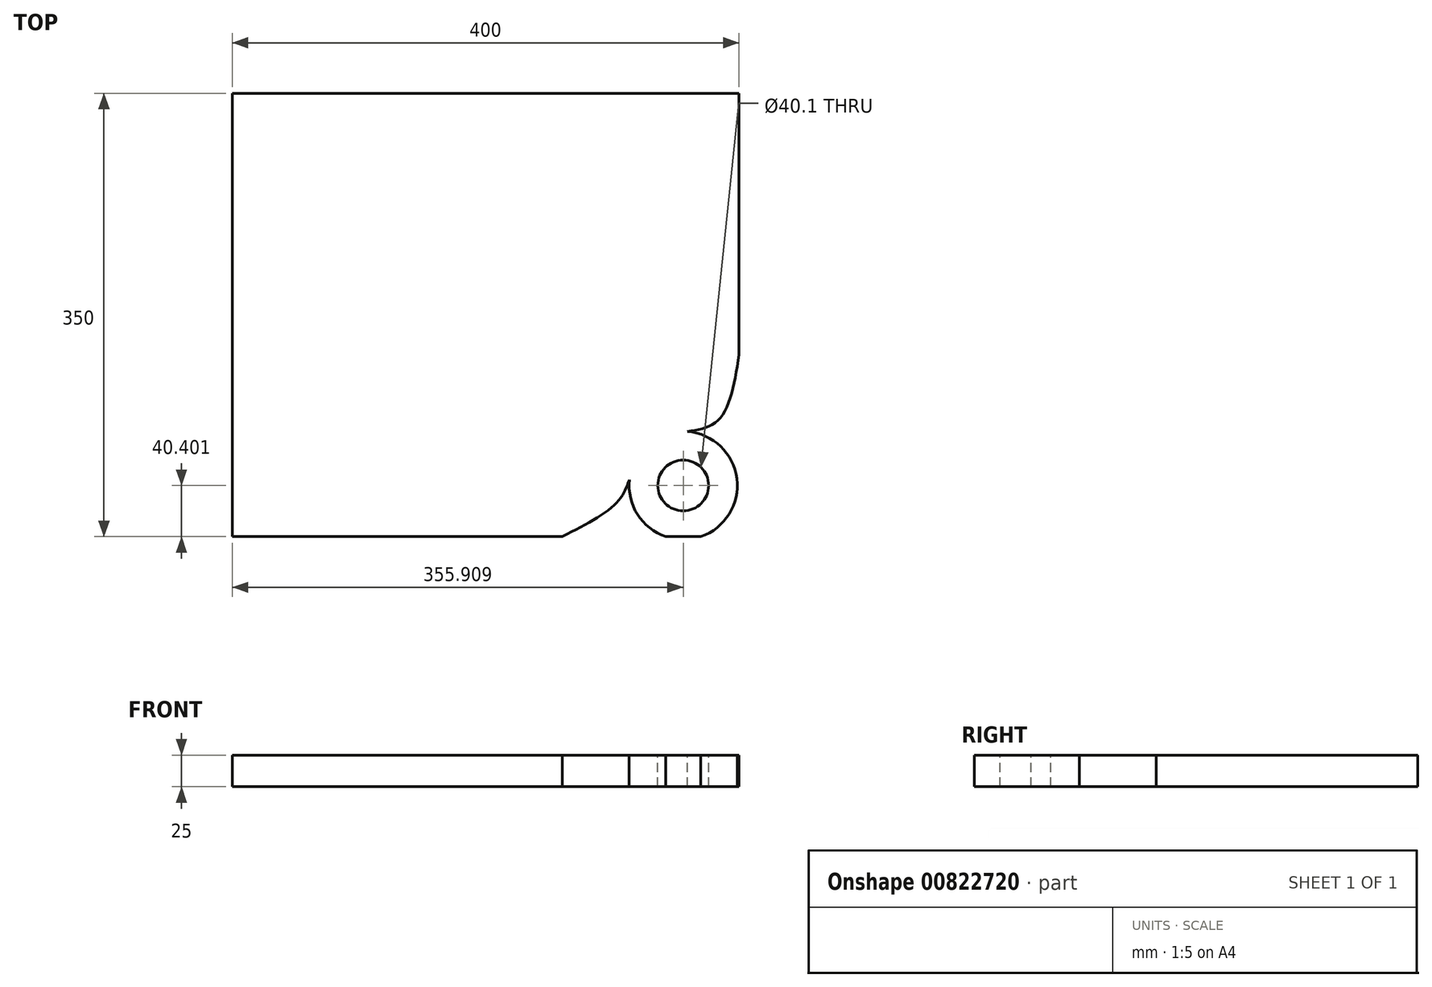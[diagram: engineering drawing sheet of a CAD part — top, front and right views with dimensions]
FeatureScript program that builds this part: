
annotation { "Feature Type Name" : "Feature", "Feature Type Description" : "" }
export const myFeature = defineFeature(function(context is Context, id is Id, definition is map)
    precondition{}
    {
        {
            var Q0;
            Q0=qCreatedBy(makeId("Top.planeOp"),FACE);
            var sketch = newSketch(context, id + "F0", { "sketchPlane" : qUnion([Q0])});
            skLineSegment(sketch, "E0.bottom", {"start": v(-344.67, 317.96) * mm, "end": v(55.33, 317.96) * mm});
            skLineSegment(sketch, "E0.top", {"start": v(-344.67, -32.04) * mm, "end": v(55.33, -32.04) * mm});
            skLineSegment(sketch, "E0.left", {"start": v(-344.67, 317.96) * mm, "end": v(-344.67, -32.04) * mm});
            skLineSegment(sketch, "E0.right", {"start": v(55.33, 317.96) * mm, "end": v(55.33, -32.04) * mm});
            skSolve(sketch);
        }
        {
            var Q0;
            Q0 = qSketchRegion(id + "F0", true);
            extrude(context, id + "F1", {"entities" : qUnion([Q0]), "depth" : 25 * mm, "offsetDistance" : 25 * mm});
        }
        {
            var Q0;
            Q0=makeQuery(id+"F1.opExtrude","CAP_FACE",FACE,{"disambiguationData":[OSD([sQuery(id+"F0.wireOp",EDGE,"E0.bottom"),sQuery(id+"F0.wireOp",EDGE,"E0.top"),sQuery(id+"F0.wireOp",EDGE,"E0.left"),sQuery(id+"F0.wireOp",EDGE,"E0.right")])],"isStart":false});
            var sketch = newSketch(context, id + "F2", { "sketchPlane" : qUnion([Q0])});
            skCircle(sketch, "E1", {"center": v(11.24, 8.36) * mm, "radius": 42.72 * mm});
            skFitSpline(sketch, "E2", {"points": [v(14.67, 50.94) * mm, v(39.8, 60.95) * mm, v(55.33, 111.58) * mm], "startDerivative": vector(67.32, 10.88) * mm, "endDerivative": vector(16.8, 105.15) * mm});
            skFitSpline(sketch, "E3", {"points": [v(-31.24, 12.86) * mm, v(-41.35, -5.27) * mm, v(-84.2, -32.04) * mm], "startDerivative": vector(-17.07, -46.93) * mm, "endDerivative": vector(-83.87, -43.14) * mm});
            skCircle(sketch, "E4", {"center": v(11.24, 8.36) * mm, "radius": 20.05 * mm});
            skSolve(sketch);
        }
        {
            var Q0;
            {var subQ0=sQuery(id+"F2.wireOp",EDGE,"E2");Q0=makeQuery(id+"F2.imprint","IMPRINT",FACE,{"disambiguationData":[TD([[makeQuery(id+"F2.imprint","IMPRINT",EDGE,{"derivedFrom":subQ0}),-1.0]])]});}
            extrude(context, id + "F3", {"entities" : qUnion([Q0]), "operationType" : NewBodyOperationType.REMOVE, "endBound" : BoundingType.THROUGH_ALL, "oppositeDirection" : true, "depth" : 25 * mm, "offsetDistance" : 25 * mm});
        }
        {
            var Q0;
            {var subQ0=sQuery(id+"F2.wireOp",EDGE,"E3");Q0=makeQuery(id+"F2.imprint","IMPRINT",FACE,{"disambiguationData":[TD([[makeQuery(id+"F2.imprint","IMPRINT",EDGE,{"derivedFrom":subQ0}),1.0]])]});}
            extrude(context, id + "F4", {"entities" : qUnion([Q0]), "operationType" : NewBodyOperationType.REMOVE, "endBound" : BoundingType.THROUGH_ALL, "oppositeDirection" : true, "depth" : 25 * mm, "offsetDistance" : 25 * mm});
        }
        {
            var Q0;
            Q0=makeQuery(id+"F2.imprint","IMPRINT",FACE,{"disambiguationData":[TD([[makeQuery(id+"F2.imprint","IMPRINT",EDGE,{"derivedFrom":sQuery(id+"F2.wireOp",EDGE,"E4")}),1.0]])]});
            extrude(context, id + "F5", {"entities" : qUnion([Q0]), "operationType" : NewBodyOperationType.REMOVE, "endBound" : BoundingType.THROUGH_ALL, "oppositeDirection" : true, "depth" : 25 * mm, "offsetDistance" : 25 * mm});
        }
    });
